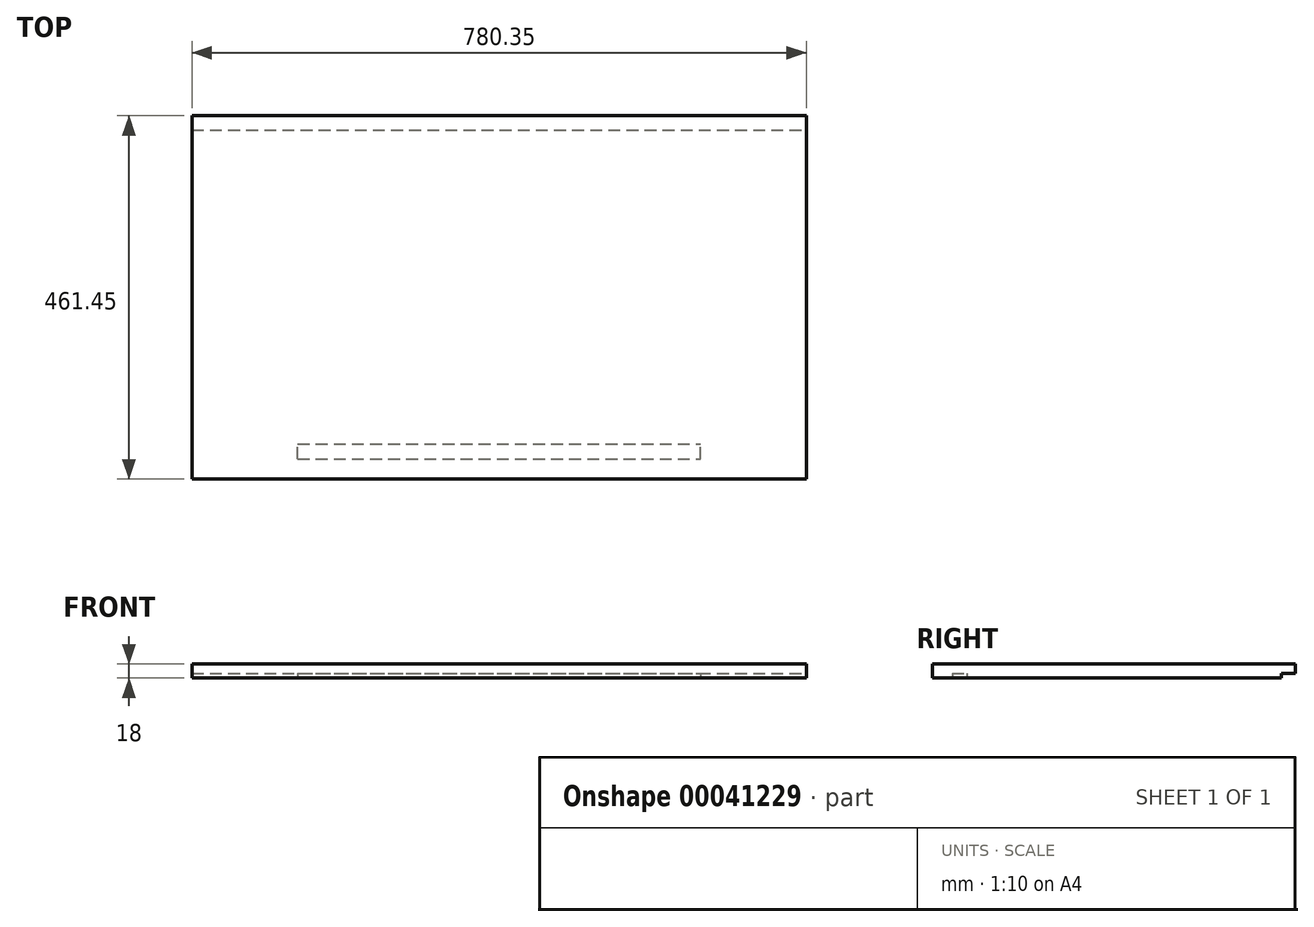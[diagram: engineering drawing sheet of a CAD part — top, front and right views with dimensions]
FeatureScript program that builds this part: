
annotation { "Feature Type Name" : "Feature", "Feature Type Description" : "" }
export const myFeature = defineFeature(function(context is Context, id is Id, definition is map)
    precondition{}
    {
        {
            var Q0;
            Q0=qCreatedBy(makeId("Top.planeOp"),FACE);
            var sketch = newSketch(context, id + "F0", { "sketchPlane" : qUnion([Q0])});
            skLineSegment(sketch, "E0.bottom", {"start": v(-389.47, 178.33) * mm, "end": v(390.88, 178.33) * mm});
            skLineSegment(sketch, "E0.top", {"start": v(-389.47, -283.12) * mm, "end": v(390.88, -283.12) * mm});
            skLineSegment(sketch, "E0.left", {"start": v(-389.47, 178.33) * mm, "end": v(-389.47, -283.12) * mm});
            skLineSegment(sketch, "E0.right", {"start": v(390.88, 178.33) * mm, "end": v(390.88, -283.12) * mm});
            skSolve(sketch);
        }
        {
            var Q0;
            Q0 = qSketchRegion(id + "F0", true);
            extrude(context, id + "F1", {"entities" : qUnion([Q0]), "depth" : 18 * mm});
        }
        {
            var Q0;
            Q0=makeQuery(id+"F1.opExtrude","CAP_FACE",FACE,{"disambiguationData":[OSD([sQuery(id+"F0.wireOp",EDGE,"E0.bottom"),sQuery(id+"F0.wireOp",EDGE,"E0.top"),sQuery(id+"F0.wireOp",EDGE,"E0.left"),sQuery(id+"F0.wireOp",EDGE,"E0.right")])],"isStart":true});
            var sketch = newSketch(context, id + "F2", { "sketchPlane" : qUnion([Q0])});
            skLineSegment(sketch, "E1.bottom", {"start": v(-255.17, 257.72) * mm, "end": v(256.45, 257.72) * mm});
            skLineSegment(sketch, "E1.top", {"start": v(-255.17, 238.72) * mm, "end": v(256.45, 238.72) * mm});
            skLineSegment(sketch, "E1.left", {"start": v(-255.17, 257.72) * mm, "end": v(-255.17, 238.72) * mm});
            skLineSegment(sketch, "E1.right", {"start": v(256.45, 257.72) * mm, "end": v(256.45, 238.72) * mm});
            skLineSegment(sketch, "E2.bottom", {"start": v(-389.47, -178.33) * mm, "end": v(390.88, -178.33) * mm});
            skLineSegment(sketch, "E2.top", {"start": v(-389.47, -160.33) * mm, "end": v(390.88, -160.33) * mm});
            skLineSegment(sketch, "E2.left", {"start": v(-389.47, -178.33) * mm, "end": v(-389.47, -160.33) * mm});
            skLineSegment(sketch, "E2.right", {"start": v(390.88, -178.33) * mm, "end": v(390.88, -160.33) * mm});
            skLineSegment(sketch, "E3", {"start": v(0, -178.33) * mm, "end": v(0.7, 283.12) * mm, "construction": true});
            skSolve(sketch);
        }
        {
            var Q0;
            Q0 = qSketchRegion(id + "F2", true);
            extrude(context, id + "F3", {"entities" : qUnion([Q0]), "operationType" : NewBodyOperationType.REMOVE, "oppositeDirection" : true, "depth" : 6 * mm});
        }
    });
